# Revit family: REVIT-BRIGADE
name_source: partatom
category: Mechanical Equipment
revit_build: Autodesk Revit 2017 (Build: 20190507_1515(x64)
units: mm (PartAtom-declared; Revit-internal decimal feet)

## family parameters
Always vertical = No
Cut with Voids When Loaded = No
OmniClass Number = 23.75.00.00
OmniClass Title = Climate Control (HVAC)
Part Type = Normal
Room Calculation Point = No
Round Connector Dimension = Use Radius
Shared = No
Work Plane-Based = No

## types (1)
- 20 L 25-RGCL
    AirVentExtension = 78 1/4"
    AirVentLocationX = 3 7/8"
    AirVentLocationY = 6 3/8"
    AirVentRadius = 1"
    Assembly Code = D3020100
    BuildingReturnExtension = 78 1/2"
    BuildingReturnHeight = 46 1/2"
    BuildingReturnLength = 17 7/8"
    BuildingReturnLocationX = 5"
    BuildingReturnLocationY = 9 1/4"
    BuildingReturnNPT = 3/4"
    BuildingReturnRadius = 3/8"
    ColdWaterInletExtension = 78 1/2"
    ColdWaterInletNPT = 1"
    ColdWaterInletRadius = 1/2"
    ColdWaterInletX = 1 3/8"
    ColdWaterInletY = 4 5/8"
    CondensateOutletExtensionX = 13"
    CondensateOutletExtensionY = 28 1/8"
    CondensateOutletHeight = 4 1/4"
    CondensateOutletNPT = 3/4"
    CondensateOutletRadius = 3/8"
    ControlBoxHeight = 2 1/8"
    ControlBoxLength = 8 7/8"
    ControlBoxWidth = 4 1/8"
    Description = BRIGADE™ INSTANTANEOUS GAS CONDENSING WATER HEATER
    DoorOpeningHeight = 59"
    DoorOpeningLocation = 2 1/8"
    DoorOpeningWidth = 14"
    DrainExtension = 22 3/8"
    DrainHeight = 10 1/2"
    DrainNPT = 3/4"
    DrainPipeRadius = 3/8"
    FlueGasLocationX = 4 7/8"
    FlueGasLocationY = 10 1/8"
    FlueGasOutlet = 3 1/2"
    FlueGasOutletExtension = 75 1/2"
    FlueGasOutletRadius = 1 3/4"
    GasInletExtension = 78 1/2"
    GasInletNPT = 1/2"
    GasInletRadius = 1/4"
    GasInletX = 3"
    GasInletY = 8 1/2"
    HotOutletX = 1 3/8"
    HotOutletY = 4 5/8"
    HotWaterOutletExtension = 78 1/2"
    HotWaterOutletNPT = 1"
    HotWaterOutletRadius = 1/2"
    IntraCirculatorRadius = 3/8"
    IntraCirculatortoRear = 16 1/2"
    Manufacturer = PVI Industries, LLC
    Model = 20 L 25-RGCL
    Modeling Code = ABO090507TAS1507ABC0905
    OmniClass Code = 23.65.35.11.11
    OmniClass Title = Storage Water Heater
    OperatingWeight = 555
    Piping Material = Copper Pipe
    ReliefLocationX = 4 7/8"
    ReliefLocationY = 1 5/8"
    ReliefValveExtension = 80"
    ReliefValveNPT = 3/4"
    ReliefValveRadius = 3/8"
    RemoteAirIntake = 3 1/2"
    RemoteAirIntakeExtension = 77 3/4"
    RemoteAirIntakeRadius = 1 3/4"
    RemoteAirIntakeX = 4 1/2"
    RemoteAirIntakeY = 13"
    StorageCapacityGallons = 25 CF
    Tank Casing = Shell
    URL = www.pvi.com
    UnitDepthFront = 18 1/4"
    UnitHeight = 75"
    UnitWidth = 16"
    Version = 1.0
    Weight Units = lbs.

## geometry (parser evidence)
native form markers: Blend x10, Sweep x2
no freeform markers — native parametric forms only
